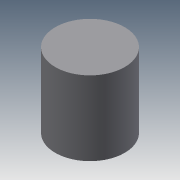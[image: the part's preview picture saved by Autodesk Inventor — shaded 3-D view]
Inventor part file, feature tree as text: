
AUTODESK INVENTOR PART (.ipt)
format: ipt  version: 2013 (Build 170138000, 138)  size: 78,848 bytes
history: native  units: mm
features: sketch x2, extrude x1, plane x1, hole x1
ambient origin geometry x8: Origin, YZ Plane, XZ Plane, XY Plane, X Axis, Y Axis, Z Axis, Center Point
bodies: Solid1 (feature_tree)
feature tree (5):
  extrude  "Extrusion1"  Depth=15.0mm TaperAngle=0.0deg
  plane  "Work Plane1"
  hole  "Hole1"  [1 undecoded]
  sketch  "Sketch1"  dims[d0=14.0mm d1=15.0mm d2=0.0mm]
  sketch  "Sketch3"  dims[d8=2.4mm d9=2.459mm d10=7.0mm d11=4.0mm d12=2.0mm d13=90.0deg d14=7.0mm d15=0.0mm]
note: 1 required parameter value undecoded (feature->parameter linkage not recoverable at this tier; creation-order binding heuristic only, values carry confidence <= 0.55)
